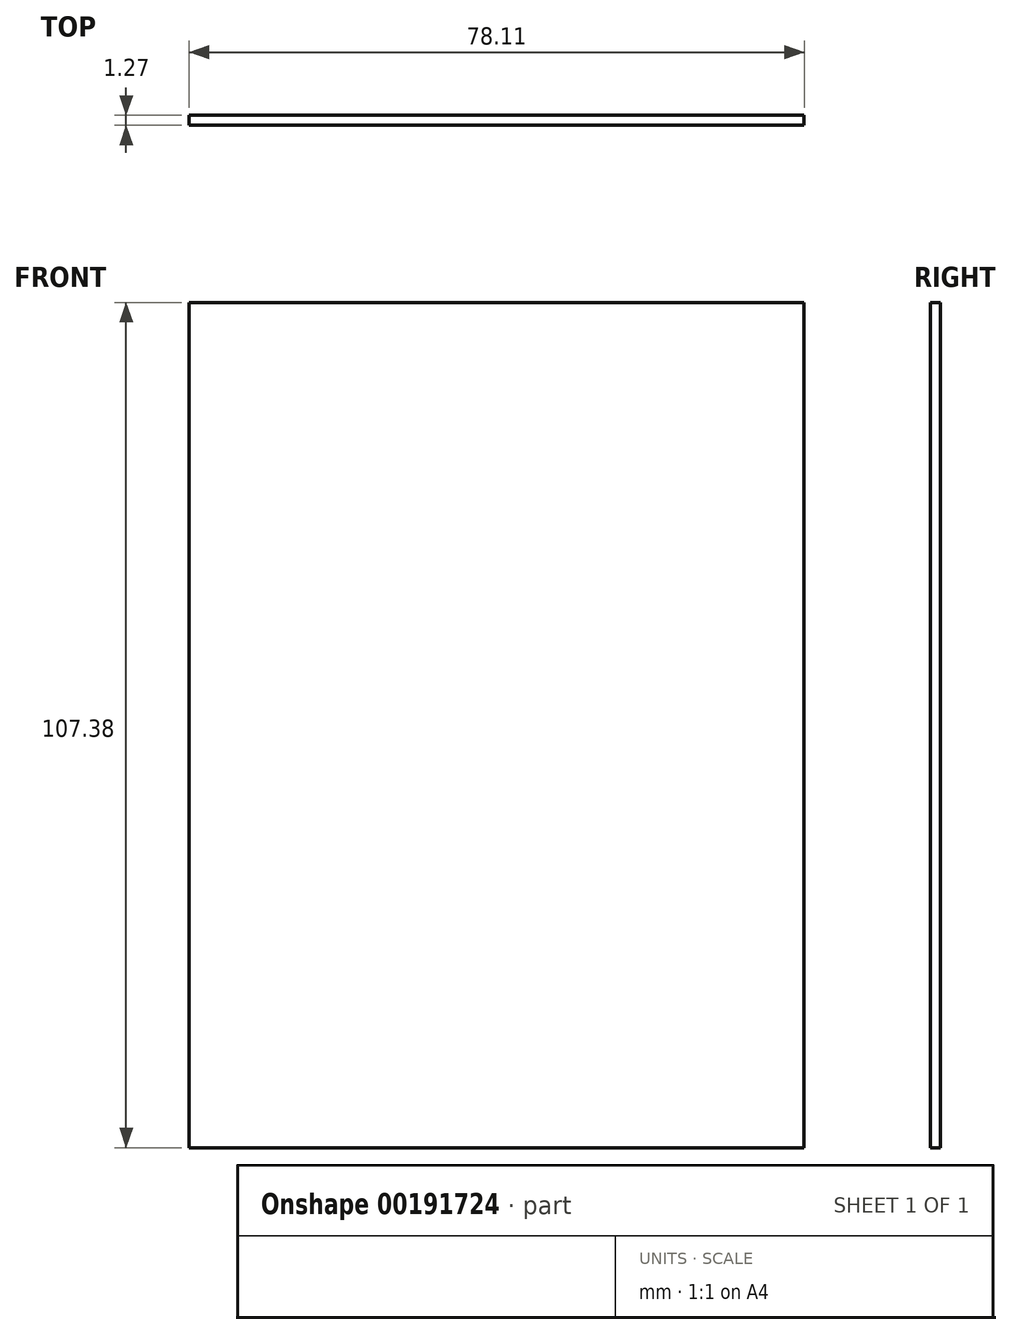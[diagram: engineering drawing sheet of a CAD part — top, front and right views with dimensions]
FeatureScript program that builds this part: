
annotation { "Feature Type Name" : "Feature", "Feature Type Description" : "" }
export const myFeature = defineFeature(function(context is Context, id is Id, definition is map)
    precondition{}
    {
        {
            var Q0;
            Q0=qCreatedBy(makeId("Front.planeOp"),FACE);
            var sketch = newSketch(context, id + "F0", { "sketchPlane" : qUnion([Q0])});
            skLineSegment(sketch, "E0.bottom", {"start": v(-54.35, 44.85) * mm, "end": v(23.76, 44.85) * mm});
            skLineSegment(sketch, "E0.top", {"start": v(-54.35, -62.53) * mm, "end": v(23.76, -62.53) * mm});
            skLineSegment(sketch, "E0.left", {"start": v(-54.35, 44.85) * mm, "end": v(-54.35, -62.53) * mm});
            skLineSegment(sketch, "E0.right", {"start": v(23.76, 44.85) * mm, "end": v(23.76, -62.53) * mm});
            skSolve(sketch);
        }
        {
            var Q0;
            Q0=makeQuery(id+"F0.imprint","IMPRINT",FACE,{"disambiguationData":[TD([[makeQuery(id+"F0.imprint","IMPRINT",EDGE,{"derivedFrom":sQuery(id+"F0.wireOp",EDGE,"E0.bottom")}),-1.0]])]});
            extrude(context, id + "F1", {"entities" : qUnion([Q0]), "depth" : 1.27 * mm});
        }
    });
